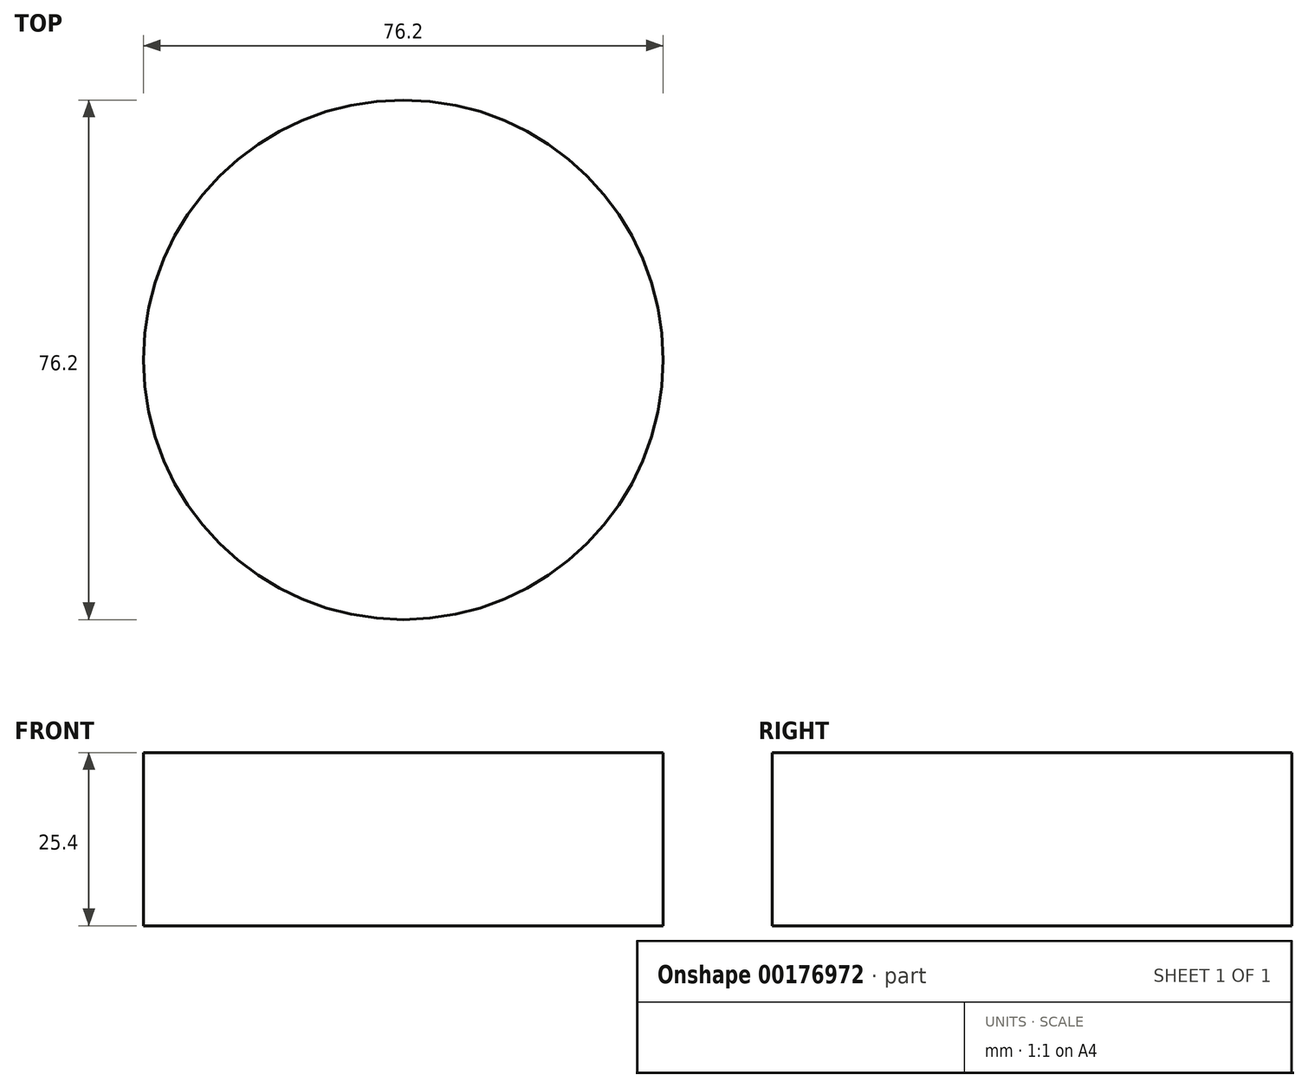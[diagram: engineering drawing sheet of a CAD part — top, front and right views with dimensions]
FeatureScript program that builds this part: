
annotation { "Feature Type Name" : "Feature", "Feature Type Description" : "" }
export const myFeature = defineFeature(function(context is Context, id is Id, definition is map)
    precondition{}
    {
        {
            var Q0;
            Q0=qCreatedBy(makeId("Top.planeOp"),FACE);
            var sketch = newSketch(context, id + "F0", { "sketchPlane" : qUnion([Q0])});
            skCircle(sketch, "E0", {"center": v(0, 0) * mm, "radius": 38.1 * mm});
            skSolve(sketch);
        }
        {
            var Q0;
            Q0=makeQuery(id+"F0.imprint","IMPRINT",FACE,{"disambiguationData":[TD([[makeQuery(id+"F0.imprint","IMPRINT",EDGE,{"derivedFrom":sQuery(id+"F0.wireOp",EDGE,"E0")}),1.0]])]});
            var sketch = newSketch(context, id + "F1", { "sketchPlane" : qUnion([Q0])});
            skSolve(sketch);
        }
        {
            var Q0;
            Q0=makeQuery(id+"F0.imprint","IMPRINT",FACE,{"disambiguationData":[TD([[makeQuery(id+"F0.imprint","IMPRINT",EDGE,{"derivedFrom":sQuery(id+"F0.wireOp",EDGE,"E0")}),1.0]])]});
            var Q1;
            Q1 = qSketchRegion(id + "F1", true);
            extrude(context, id + "F2", {"entities" : qUnion([Q0, Q1]), "depth" : 25.4 * mm});
        }
    });
